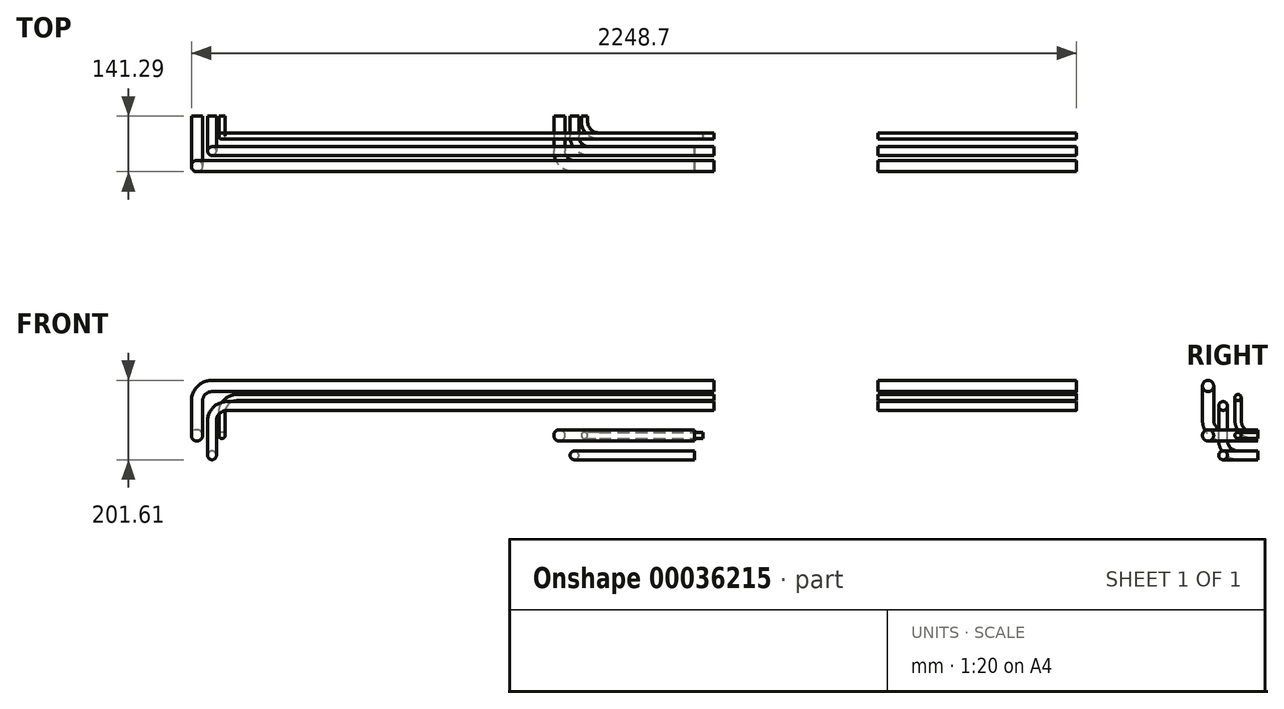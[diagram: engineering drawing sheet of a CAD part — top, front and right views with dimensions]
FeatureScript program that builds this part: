
annotation { "Feature Type Name" : "Feature", "Feature Type Description" : "" }
export const myFeature = defineFeature(function(context is Context, id is Id, definition is map)
    precondition{}
    {
        {
            var Q0;
            Q0=qCreatedBy(makeId("Front.planeOp"),FACE);
            var sketch = newSketch(context, id + "F0", { "sketchPlane" : qUnion([Q0])});
            skCircle(sketch, "E0", {"center": v(-38.1, 50.8) * mm, "radius": 14.29 * mm});
            skCircle(sketch, "E1", {"center": v(25.4, 50.8) * mm, "radius": 7.94 * mm});
            skCircle(sketch, "E2", {"center": v(0, 0) * mm, "radius": 11.11 * mm});
            skLineSegment(sketch, "E3", {"start": v(-38.1, 50.8) * mm, "end": v(25.4, 50.8) * mm, "construction": true});
            skCircle(sketch, "E4", {"center": v(882.65, 50.8) * mm, "radius": 14.29 * mm});
            skCircle(sketch, "E5", {"center": v(946.15, 50.8) * mm, "radius": 7.94 * mm});
            skCircle(sketch, "E6", {"center": v(920.75, 0) * mm, "radius": 11.11 * mm});
            skLineSegment(sketch, "E7", {"start": v(882.65, 50.8) * mm, "end": v(946.15, 50.8) * mm, "construction": true});
            skCircle(sketch, "E8", {"center": v(1803.4, 50.8) * mm, "radius": 14.29 * mm});
            skCircle(sketch, "E9", {"center": v(1866.9, 50.8) * mm, "radius": 7.94 * mm});
            skCircle(sketch, "E10", {"center": v(1841.5, 0) * mm, "radius": 11.11 * mm});
            skLineSegment(sketch, "E11", {"start": v(1803.4, 50.8) * mm, "end": v(1866.9, 50.8) * mm, "construction": true});
            skSolve(sketch);
        }
        {
            var Q0;
            Q0=sQuery(id+"F0.wireOp",VERTEX,"E0.center");
            var Q1;
            Q1=qCreatedBy(makeId("Right.planeOp"),FACE);
            cPlane(context, id + "F1", {"entities" : qUnion([Q0, Q1]), "cplaneType" : CPlaneType.PLANE_POINT, "offset" : 152.4 * mm, "width" : 152.4 * mm, "height" : 152.4 * mm});
        }
        {
            var Q0;
            Q0=qCreatedBy(makeId("Right.planeOp"),FACE);
            var Q1;
            Q1=sQuery(id+"F0.wireOp",VERTEX,"E1.center");
            cPlane(context, id + "F2", {"entities" : qUnion([Q0, Q1]), "cplaneType" : CPlaneType.PLANE_POINT, "offset" : 152.4 * mm, "width" : 152.4 * mm, "height" : 152.4 * mm});
        }
        {
            var Q0;
            Q0=qCreatedBy(makeId("Top.planeOp"),FACE);
            var Q1;
            Q1=sQuery(id+"F0.wireOp",VERTEX,"E1.center");
            cPlane(context, id + "F3", {"entities" : qUnion([Q0, Q1]), "cplaneType" : CPlaneType.PLANE_POINT, "offset" : 152.4 * mm, "width" : 152.4 * mm, "height" : 152.4 * mm});
        }
        {
            var Q0;
            Q0=qCreatedBy(makeId("Front.planeOp"),FACE);
            var sketch = newSketch(context, id + "F4", { "sketchPlane" : qUnion([Q0])});
            skLineSegment(sketch, "E12", {"start": v(2168.53, 50.8) * mm, "end": v(2310.6, 50.8) * mm, "construction": true});
            skLineSegment(sketch, "E13", {"start": v(2310.6, 50.8) * mm, "end": v(2432.05, 146.84) * mm, "construction": true});
            skLineSegment(sketch, "E14", {"start": v(2432.05, 146.84) * mm, "end": v(2612.23, 146.84) * mm, "construction": true});
            skLineSegment(sketch, "E15", {"start": v(2432.05, 146.84) * mm, "end": v(2196.3, 146.84) * mm, "construction": true});
            skLineSegment(sketch, "E16", {"start": v(2146.3, 50.8) * mm, "end": v(2310.6, 50.8) * mm, "construction": true});
            skLineSegment(sketch, "E17", {"start": v(2310.6, 50.8) * mm, "end": v(2462.21, 176.21) * mm, "construction": true});
            skLineSegment(sketch, "E18", {"start": v(2462.21, 176.21) * mm, "end": v(2663.03, 176.21) * mm, "construction": true});
            skLineSegment(sketch, "E19", {"start": v(2462.21, 176.21) * mm, "end": v(2192.34, 176.21) * mm, "construction": true});
            skLineSegment(sketch, "E20", {"start": v(2462.21, 125.41) * mm, "end": v(2663.03, 125.41) * mm, "construction": true});
            skLineSegment(sketch, "E21", {"start": v(2462.21, 125.41) * mm, "end": v(2192.34, 125.41) * mm, "construction": true});
            skLineSegment(sketch, "E22", {"start": v(2310.6, 0) * mm, "end": v(2462.21, 125.41) * mm, "construction": true});
            skLineSegment(sketch, "E23", {"start": v(2146.3, 0) * mm, "end": v(2310.6, 0) * mm, "construction": true});
            skLineSegment(sketch, "E24", {"start": v(1541.46, 125.41) * mm, "end": v(1742.28, 125.41) * mm, "construction": true});
            skLineSegment(sketch, "E25", {"start": v(1541.46, 125.41) * mm, "end": v(1271.59, 125.41) * mm, "construction": true});
            skLineSegment(sketch, "E26", {"start": v(1389.86, 0) * mm, "end": v(1541.46, 125.41) * mm, "construction": true});
            skLineSegment(sketch, "E27", {"start": v(1247.78, 50.8) * mm, "end": v(1389.86, 50.8) * mm, "construction": true});
            skLineSegment(sketch, "E28", {"start": v(1541.46, 176.21) * mm, "end": v(1271.59, 176.21) * mm, "construction": true});
            skLineSegment(sketch, "E29", {"start": v(1541.46, 176.21) * mm, "end": v(1742.28, 176.21) * mm, "construction": true});
            skLineSegment(sketch, "E30", {"start": v(1389.86, 50.8) * mm, "end": v(1541.46, 176.21) * mm, "construction": true});
            skLineSegment(sketch, "E31", {"start": v(1225.55, 50.8) * mm, "end": v(1389.86, 50.8) * mm, "construction": true});
            skLineSegment(sketch, "E32", {"start": v(1511.3, 146.84) * mm, "end": v(1275.56, 146.84) * mm, "construction": true});
            skLineSegment(sketch, "E33", {"start": v(1511.3, 146.84) * mm, "end": v(1691.48, 146.84) * mm, "construction": true});
            skLineSegment(sketch, "E34", {"start": v(1389.86, 50.8) * mm, "end": v(1511.3, 146.84) * mm, "construction": true});
            skLineSegment(sketch, "E35", {"start": v(1225.55, 0) * mm, "end": v(1389.86, 0) * mm, "construction": true});
            skLineSegment(sketch, "E36", {"start": v(2196.3, 146.84) * mm, "end": v(1691.48, 146.84) * mm});
            skLineSegment(sketch, "E37", {"start": v(1742.28, 125.41) * mm, "end": v(2192.34, 125.41) * mm});
            skLineSegment(sketch, "E38", {"start": v(2192.34, 176.21) * mm, "end": v(1742.28, 176.21) * mm});
            skLineSegment(sketch, "E39", {"start": v(1271.59, 125.41) * mm, "end": v(0, 125.41) * mm});
            skLineSegment(sketch, "E40", {"start": v(1275.56, 146.84) * mm, "end": v(25.4, 146.84) * mm});
            skLineSegment(sketch, "E41", {"start": v(1271.59, 176.21) * mm, "end": v(-38.1, 176.21) * mm});
            skLineSegment(sketch, "E42", {"start": v(-38.1, 176.21) * mm, "end": v(-38.1, 50.8) * mm});
            skLineSegment(sketch, "E43", {"start": v(25.4, 146.84) * mm, "end": v(25.4, 50.8) * mm});
            skLineSegment(sketch, "E44", {"start": v(0, 125.41) * mm, "end": v(0, 0) * mm});
            skSolve(sketch);
        }
        {
            var Q0;
            Q0=qCreatedBy(makeId("Right.planeOp"),FACE);
            var sketch = newSketch(context, id + "F5", { "sketchPlane" : qUnion([Q0])});
            skLineSegment(sketch, "E45", {"start": v(0, 0) * mm, "end": v(-50.8, 0) * mm});
            skArc(sketch, "E46", {"start": v(-50.8, 0) * mm, "mid": v(-77.74, 11.16) * mm, "end": v(-88.9, 38.1) * mm});
            skLineSegment(sketch, "E47", {"start": v(-88.9, 38.1) * mm, "end": v(-88.9, 87.31) * mm});
            skLineSegment(sketch, "E48", {"start": v(-153.28, 125.41) * mm, "end": v(-127, 125.41) * mm, "construction": true});
            skPoint(sketch, "E49.visualSharp", {"position": v(-88.9, 125.41) * mm});
            skArc(sketch, "E49.filletArc", {"start": v(-88.9, 87.31) * mm, "mid": v(-100.06, 114.25) * mm, "end": v(-127, 125.41) * mm, "construction": true});
            skSolve(sketch);
        }
        {
            var Q0;
            Q0=qCreatedBy(makeId("Front.planeOp"),FACE);
            var Q1;
            Q1=sQuery(id+"F5.wireOp",VERTEX,"E49.filletArc.start");
            cPlane(context, id + "F6", {"entities" : qUnion([Q0, Q1]), "cplaneType" : CPlaneType.PLANE_POINT, "offset" : 152.4 * mm, "width" : 152.4 * mm, "height" : 152.4 * mm});
        }
        {
            var Q0;
            Q0=qCreatedBy(id+"F6.planeOp",FACE);
            var sketch = newSketch(context, id + "F7", { "sketchPlane" : qUnion([Q0])});
            skArc(sketch, "E50", {"start": v(38.1, 125.41) * mm, "mid": v(11.16, 114.25) * mm, "end": v(0, 87.31) * mm});
            skLineSegment(sketch, "E51", {"start": v(38.1, 125.41) * mm, "end": v(1275.56, 125.41) * mm});
            skLineSegment(sketch, "E52", {"start": v(1275.56, 125.41) * mm, "end": v(2196.3, 125.41) * mm});
            skSolve(sketch);
        }
        {
            var Q0;
            Q0=makeQuery(id+"F0.imprint","IMPRINT",FACE,{"disambiguationData":[TD([[makeQuery(id+"F0.imprint","IMPRINT",EDGE,{"derivedFrom":sQuery(id+"F0.wireOp",EDGE,"E2")}),1.0]])]});
            var Q1;
            Q1=sQuery(id+"F5.wireOp",EDGE,"E45");
            var Q2;
            Q2=sQuery(id+"F5.wireOp",EDGE,"E46");
            var Q3;
            Q3=sQuery(id+"F5.wireOp",EDGE,"E47");
            var Q4;
            Q4=sQuery(id+"F7.wireOp",EDGE,"E50");
            var Q5;
            Q5=sQuery(id+"F7.wireOp",EDGE,"E51");
            var Q6;
            Q6=sQuery(id+"F7.wireOp",EDGE,"E52");
            sweep(context, id + "F8", {"profiles" : qUnion([Q0]), "path" : qUnion([Q1, Q2, Q3, Q4, Q5, Q6])});
        }
        {
            var Q0;
            Q0=qCreatedBy(id+"F1.planeOp",FACE);
            var sketch = newSketch(context, id + "F9", { "sketchPlane" : qUnion([Q0])});
            skLineSegment(sketch, "E53", {"start": v(0, 50.8) * mm, "end": v(-88.9, 50.8) * mm});
            skArc(sketch, "E54", {"start": v(-88.9, 50.8) * mm, "mid": v(-115.84, 61.96) * mm, "end": v(-127, 88.9) * mm});
            skLineSegment(sketch, "E55", {"start": v(-127, 88.9) * mm, "end": v(-127, 138.11) * mm});
            skLineSegment(sketch, "E56", {"start": v(-111.3, 176.21) * mm, "end": v(-165.1, 176.21) * mm, "construction": true});
            skPoint(sketch, "E57.visualSharp", {"position": v(-127, 176.21) * mm});
            skArc(sketch, "E57.filletArc", {"start": v(-127, 138.11) * mm, "mid": v(-138.16, 165.05) * mm, "end": v(-165.1, 176.21) * mm, "construction": true});
            skSolve(sketch);
        }
        {
            var Q0;
            Q0=qCreatedBy(id+"F6.planeOp",FACE);
            var Q1;
            Q1=sQuery(id+"F9.wireOp",VERTEX,"E57.filletArc.start");
            cPlane(context, id + "F10", {"entities" : qUnion([Q0, Q1]), "cplaneType" : CPlaneType.PLANE_POINT, "offset" : 152.4 * mm, "width" : 152.4 * mm, "height" : 152.4 * mm});
        }
        {
            var Q0;
            Q0=qCreatedBy(id+"F10.planeOp",FACE);
            var sketch = newSketch(context, id + "F11", { "sketchPlane" : qUnion([Q0])});
            skArc(sketch, "E58", {"start": v(0, 176.21) * mm, "mid": v(-26.94, 165.05) * mm, "end": v(-38.1, 138.11) * mm});
            skLineSegment(sketch, "E59", {"start": v(0, 176.21) * mm, "end": v(1275.56, 176.21) * mm});
            skLineSegment(sketch, "E60", {"start": v(1275.56, 176.21) * mm, "end": v(2196.3, 176.21) * mm});
            skSolve(sketch);
        }
        {
            var Q0;
            Q0=makeQuery(id+"F0.imprint","IMPRINT",FACE,{"disambiguationData":[TD([[makeQuery(id+"F0.imprint","IMPRINT",EDGE,{"derivedFrom":sQuery(id+"F0.wireOp",EDGE,"E0")}),1.0]])]});
            var Q1;
            Q1=sQuery(id+"F9.wireOp",EDGE,"E53");
            var Q2;
            Q2=sQuery(id+"F9.wireOp",EDGE,"E54");
            var Q3;
            Q3=sQuery(id+"F9.wireOp",EDGE,"E55");
            var Q4;
            Q4=sQuery(id+"F11.wireOp",EDGE,"E58");
            var Q5;
            Q5=sQuery(id+"F11.wireOp",EDGE,"E59");
            var Q6;
            Q6=sQuery(id+"F11.wireOp",EDGE,"E60");
            sweep(context, id + "F12", {"profiles" : qUnion([Q0]), "path" : qUnion([Q1, Q2, Q3, Q4, Q5, Q6])});
        }
        {
            var Q0;
            Q0=qCreatedBy(id+"F2.planeOp",FACE);
            var sketch = newSketch(context, id + "F13", { "sketchPlane" : qUnion([Q0])});
            skLineSegment(sketch, "E61", {"start": v(0, 50.8) * mm, "end": v(-12.7, 50.8) * mm});
            skLineSegment(sketch, "E62", {"start": v(-50.8, 88.9) * mm, "end": v(-50.8, 108.74) * mm});
            skLineSegment(sketch, "E63", {"start": v(-88.9, 146.84) * mm, "end": v(-132, 146.84) * mm, "construction": true});
            skPoint(sketch, "E64.visualSharp", {"position": v(-50.8, 50.8) * mm});
            skArc(sketch, "E64.filletArc", {"start": v(-50.8, 88.9) * mm, "mid": v(-39.64, 61.96) * mm, "end": v(-12.7, 50.8) * mm});
            skPoint(sketch, "E65.visualSharp", {"position": v(-50.8, 146.84) * mm});
            skArc(sketch, "E65.filletArc", {"start": v(-50.8, 108.74) * mm, "mid": v(-61.96, 135.68) * mm, "end": v(-88.9, 146.84) * mm, "construction": true});
            skSolve(sketch);
        }
        {
            var Q0;
            Q0=qCreatedBy(makeId("Front.planeOp"),FACE);
            var Q1;
            Q1=sQuery(id+"F13.wireOp",VERTEX,"E62.end");
            cPlane(context, id + "F14", {"entities" : qUnion([Q0, Q1]), "cplaneType" : CPlaneType.PLANE_POINT, "offset" : 152.4 * mm, "width" : 152.4 * mm, "height" : 152.4 * mm});
        }
        {
            var Q0;
            Q0=qCreatedBy(id+"F14.planeOp",FACE);
            var sketch = newSketch(context, id + "F15", { "sketchPlane" : qUnion([Q0])});
            skArc(sketch, "E66", {"start": v(63.5, 146.84) * mm, "mid": v(36.56, 135.68) * mm, "end": v(25.4, 108.74) * mm});
            skLineSegment(sketch, "E67", {"start": v(63.5, 146.84) * mm, "end": v(1275.56, 146.84) * mm});
            skLineSegment(sketch, "E68", {"start": v(1275.56, 146.84) * mm, "end": v(2196.3, 146.84) * mm});
            skSolve(sketch);
        }
        {
            var Q0;
            Q0=makeQuery(id+"F0.imprint","IMPRINT",FACE,{"disambiguationData":[TD([[makeQuery(id+"F0.imprint","IMPRINT",EDGE,{"derivedFrom":sQuery(id+"F0.wireOp",EDGE,"E1")}),1.0]])]});
            var Q1;
            Q1=sQuery(id+"F13.wireOp",EDGE,"E61");
            var Q2;
            Q2=sQuery(id+"F13.wireOp",EDGE,"E64.filletArc");
            var Q3;
            Q3=sQuery(id+"F13.wireOp",EDGE,"E62");
            var Q4;
            Q4=sQuery(id+"F15.wireOp",EDGE,"E66");
            var Q5;
            Q5=sQuery(id+"F15.wireOp",EDGE,"E67");
            var Q6;
            Q6=sQuery(id+"F15.wireOp",EDGE,"E68");
            sweep(context, id + "F16", {"profiles" : qUnion([Q0]), "path" : qUnion([Q1, Q2, Q3, Q4, Q5, Q6])});
        }
        {
            var Q0;
            Q0=qCreatedBy(id+"F3.planeOp",FACE);
            var sketch = newSketch(context, id + "F17", { "sketchPlane" : qUnion([Q0])});
            skLineSegment(sketch, "E69", {"start": v(946.15, 0) * mm, "end": v(946.15, -12.7) * mm});
            skLineSegment(sketch, "E70", {"start": v(882.65, 0) * mm, "end": v(882.65, -88.9) * mm});
            skArc(sketch, "E71", {"start": v(882.65, -88.9) * mm, "mid": v(893.8, -115.84) * mm, "end": v(920.75, -127) * mm});
            skArc(sketch, "E72", {"start": v(946.15, -12.7) * mm, "mid": v(957.3, -39.64) * mm, "end": v(984.25, -50.8) * mm});
            skLineSegment(sketch, "E73", {"start": v(920.75, 0) * mm, "end": v(920.75, -50.8) * mm});
            skArc(sketch, "E74", {"start": v(920.75, -50.8) * mm, "mid": v(931.9, -77.74) * mm, "end": v(958.85, -88.9) * mm});
            skLineSegment(sketch, "E75", {"start": v(984.25, -50.8) * mm, "end": v(1247.78, -50.8) * mm});
            skLineSegment(sketch, "E76", {"start": v(958.85, -88.9) * mm, "end": v(1225.55, -88.9) * mm});
            skLineSegment(sketch, "E77", {"start": v(920.75, -127) * mm, "end": v(1225.55, -127) * mm});
            skSolve(sketch);
        }
        {
            var Q0;
            Q0=makeQuery(id+"F0.imprint","IMPRINT",FACE,{"disambiguationData":[TD([[makeQuery(id+"F0.imprint","IMPRINT",EDGE,{"derivedFrom":sQuery(id+"F0.wireOp",EDGE,"E5")}),1.0]])]});
            var Q1;
            Q1=sQuery(id+"F17.wireOp",EDGE,"E69");
            var Q2;
            Q2=sQuery(id+"F17.wireOp",EDGE,"E72");
            var Q3;
            Q3=sQuery(id+"F17.wireOp",EDGE,"E75");
            sweep(context, id + "F18", {"profiles" : qUnion([Q0]), "path" : qUnion([Q1, Q2, Q3])});
        }
        {
            var Q0;
            Q0=makeQuery(id+"F0.imprint","IMPRINT",FACE,{"disambiguationData":[TD([[makeQuery(id+"F0.imprint","IMPRINT",EDGE,{"derivedFrom":sQuery(id+"F0.wireOp",EDGE,"E6")}),1.0]])]});
            var Q1;
            Q1=sQuery(id+"F17.wireOp",EDGE,"E73");
            var Q2;
            Q2=sQuery(id+"F17.wireOp",EDGE,"E74");
            var Q3;
            Q3=sQuery(id+"F17.wireOp",EDGE,"E76");
            sweep(context, id + "F19", {"profiles" : qUnion([Q0]), "path" : qUnion([Q1, Q2, Q3])});
        }
        {
            var Q0;
            Q0=makeQuery(id+"F0.imprint","IMPRINT",FACE,{"disambiguationData":[TD([[makeQuery(id+"F0.imprint","IMPRINT",EDGE,{"derivedFrom":sQuery(id+"F0.wireOp",EDGE,"E4")}),1.0]])]});
            var Q1;
            Q1=sQuery(id+"F17.wireOp",EDGE,"E70");
            var Q2;
            Q2=sQuery(id+"F17.wireOp",EDGE,"E77");
            var Q3;
            Q3=sQuery(id+"F17.wireOp",EDGE,"E71");
            sweep(context, id + "F20", {"profiles" : qUnion([Q0]), "path" : qUnion([Q1, Q2, Q3])});
        }
        {
            var Q0;
            Q0=qCreatedBy(makeId("Front.planeOp"),FACE);
            var sketch = newSketch(context, id + "F21", { "sketchPlane" : qUnion([Q0])});
            skLineSegment(sketch, "E78.bottom", {"start": v(1275.56, 273.84) * mm, "end": v(1691.48, 273.84) * mm});
            skLineSegment(sketch, "E78.top", {"start": v(1275.56, 19.84) * mm, "end": v(1691.48, 19.84) * mm});
            skLineSegment(sketch, "E78.left", {"start": v(1275.56, 273.84) * mm, "end": v(1275.56, 19.84) * mm});
            skLineSegment(sketch, "E78.right", {"start": v(1691.48, 273.84) * mm, "end": v(1691.48, 19.84) * mm});
            skSolve(sketch);
        }
        {
            var Q0;
            Q0 = qSketchRegion(id + "F21", true);
            extrude(context, id + "F22", {"entities" : qUnion([Q0]), "operationType" : NewBodyOperationType.REMOVE, "endBound" : BoundingType.THROUGH_ALL, "depth" : 25.4 * mm});
        }
    });
